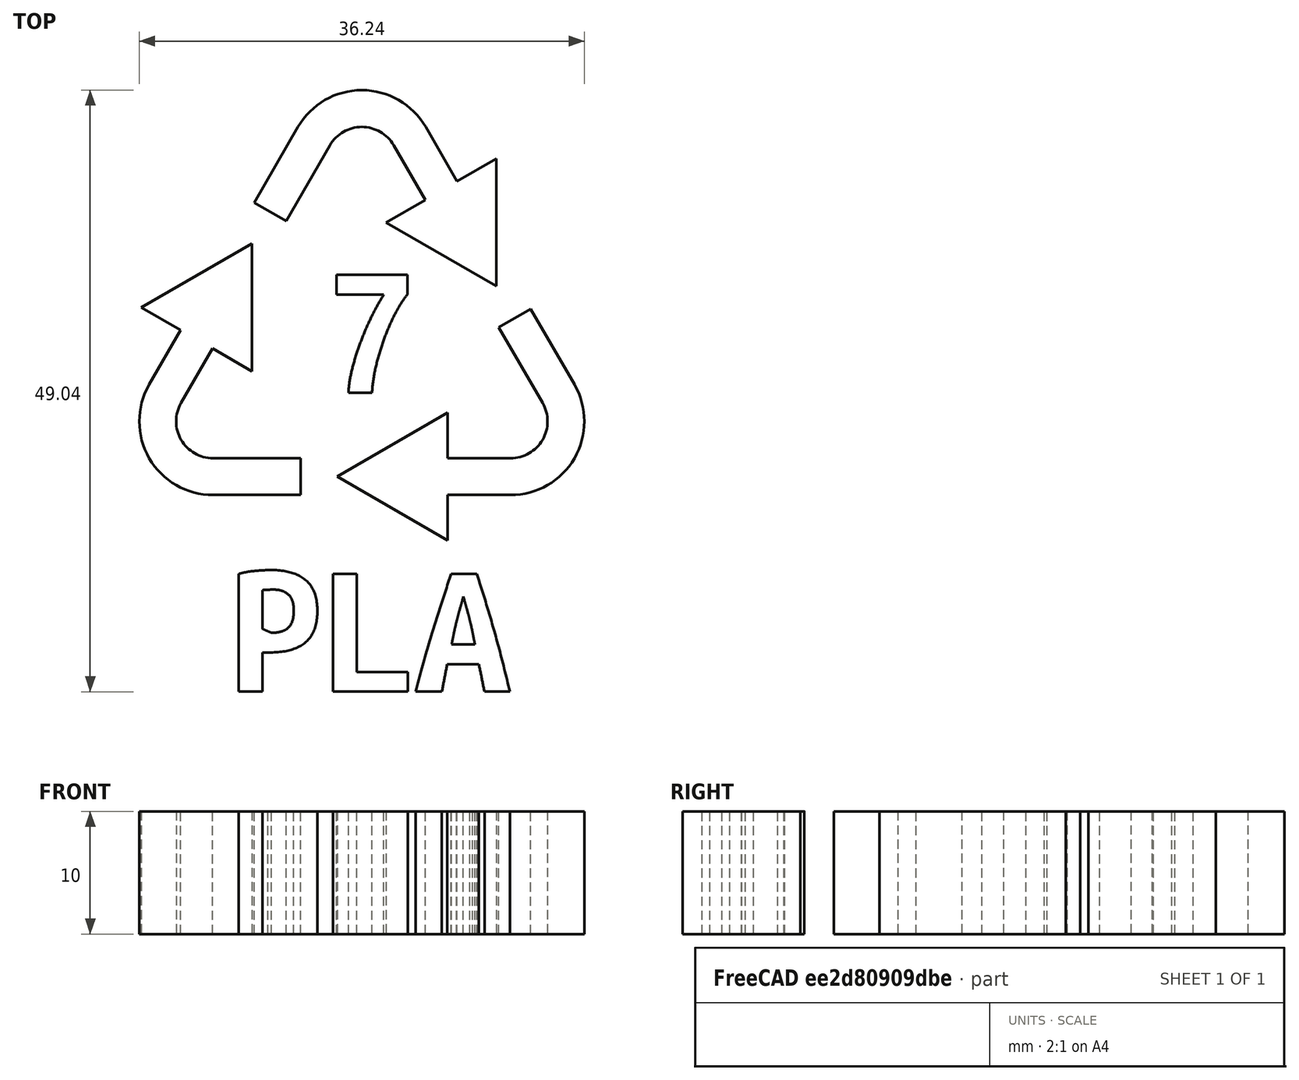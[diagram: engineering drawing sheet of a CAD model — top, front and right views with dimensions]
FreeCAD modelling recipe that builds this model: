
FCSTD DOCUMENT  (FreeCAD 0.17R13541 (Git))
Label: PLA-recycling-symbol
License: All rights reserved
LicenseURL: http://en.wikipedia.org/wiki/All_rights_reserved
objects: Part::Extrusion×5, Part::Fillet×5, Part::Feature×4, Part::MultiFuse×4, Part::RegularPolygon×3, Part::Part2DObjectPython×2, Part::Cut×2, Part::FeaturePython×2, Part::Box×1, App::DocumentObjectGroup×1
note: 28 computed .brp shape members not serialized (recipe doc carries the construction recipe); baked Part::Feature solids carry a one-line shape summary decoded from their .brp

FEATURE [Part::Part2DObjectPython] ShapeString  # Draft 2D object (typed FeaturePython)
  FontFile = <userpath>/Desktop/rrlOwncloud/Libraries-and-settings/Fonts/ubuntu-font-family-0.80/UbuntuMono-B.ttf
  Placement = pos=(-45.93,-118.03,0) rot=(0.707107,-0.707107,0;3.14159rad)
  Size = 10
  String = PLA
  Tracking = 0
FEATURE [Part::Extrusion] Extrude  label="PLA-1"
  Base = -> ShapeString
  Dir = (0,0,-1)
  DirMode = 2
  FaceMakerClass = Part::FaceMakerBullseye
  LengthFwd = 10
  LengthRev = 0
  Placement = pos=(-142,-85,0) rot=(-0.707107,0.707107,0;3.14159rad)
  Solid = false
  Symmetric = false
FEATURE [Part::Part2DObjectPython] ShapeString001  # Draft 2D object (typed FeaturePython)
  FontFile = <userpath>/Desktop/rrlOwncloud/Libraries-and-settings/Fonts/ubuntu-font-family-0.80/UbuntuMono-B.ttf
  Placement = pos=(87.32,101.38,0) rot=(0.707107,-0.707107,0;3.14159rad)
  Size = 10
  String = 7
  Tracking = 0
FEATURE [Part::Extrusion] Extrude001  label="7-1"
  Base = -> ShapeString001
  Dir = (0,0,-1)
  DirMode = 2
  FaceMakerClass = Part::FaceMakerBullseye
  LengthFwd = 10
  LengthRev = 0
  Placement = pos=(95,78,0) rot=(-0.707107,0.707107,0;3.14159rad)
  Solid = false
  Symmetric = false
FEATURE [Part::RegularPolygon] RegularPolygon  label="Regular polygon"
  AttacherType = Attacher::AttachEngine3D
  Circumradius = 20
  Placement = pos=(0,0,0) rot=(0,0,1;1.5708rad)
  Polygon = 3
FEATURE [Part::RegularPolygon] RegularPolygon001  label="Regular polygon001"
  AttacherType = Attacher::AttachEngine3D
  Circumradius = 26
  Placement = pos=(0,0,0) rot=(0,0,1;1.5708rad)
  Polygon = 3
FEATURE [Part::Extrusion] Extrude002
  Base = -> RegularPolygon001
  Dir = (0,0,1)
  DirMode = 2
  FaceMakerClass = Part::FaceMakerBullseye
  LengthFwd = 10
  LengthRev = 0
  Solid = true
  Symmetric = false
FEATURE [Part::Extrusion] Extrude003
  Base = -> RegularPolygon
  Dir = (0,0,1)
  DirMode = 2
  FaceMakerClass = Part::FaceMakerBullseye
  LengthFwd = 12
  LengthRev = 0
  Placement = pos=(0,0,-1) rot=(0,0,1;0rad)
  Solid = true
  Symmetric = false
FEATURE [Part::Cut] Cut
  Base = -> Extrude002
  Tool = -> Extrude003
FEATURE [Part::Fillet] Fillet
  Base = -> Cut
  Edges = 1 edges r=3: [Edge18]
FEATURE [Part::Fillet] Fillet001
  Base = -> Fillet
  Edges = 1 edges r=6: [Edge16]
FEATURE [Part::Fillet] Fillet002
  Base = -> Fillet001
  Edges = 1 edges r=3: [Edge18]
FEATURE [Part::Fillet] Fillet003
  Base = -> Fillet002
  Edges = 1 edges r=3: [Edge17]
FEATURE [Part::Fillet] Fillet004  label="triangle-ring"
  Base = -> Fillet003
  Edges = 2 edges r=6: [Edge24,Edge28]
FEATURE [Part::RegularPolygon] RegularPolygon002  label="Regular polygon002"
  AttacherType = Attacher::AttachEngine3D
  Circumradius = 6
  Polygon = 3
FEATURE [Part::Extrusion] Extrude004  label="arrow"
  Base = -> RegularPolygon002
  Dir = (0,0,1)
  DirMode = 2
  FaceMakerClass = Part::FaceMakerBullseye
  LengthFwd = 10
  LengthRev = 0
  Placement = pos=(-4,-11.5,0) rot=(0,0,1;0rad)
  Solid = true
  Symmetric = false
FEATURE [Part::Feature] Extrude004001
  Placement = pos=(11.9593,2.2859,0) rot=(0,0,1;2.0944rad)
  shape: bbox 9 x 10.39 x 10 mm, 5 faces (baked)
FEATURE [Part::Feature] Extrude004002
  Placement = pos=(-7.95929,9.2141,0) rot=(0,0,1;4.18879rad)
  shape: bbox 9 x 10.39 x 10 mm, 5 faces (baked)
FEATURE [Part::Box] Box001  label="Cube001"
  AttacherType = Attacher::AttachEngine3D
  Height = 16
  Length = 10
  Placement = pos=(-5,-17,-4) rot=(0,0,1;0rad)
  Width = 10
FEATURE [Part::Feature] Box001001
  Placement = pos=(17.2224,4.16987,-4) rot=(0,0,1;2.0944rad)
  shape: bbox 13.66 x 13.66 x 16 mm, 6 faces (baked)
FEATURE [Part::Feature] Box001002
  Placement = pos=(-12.2224,12.8301,-4) rot=(0,0,1;4.18879rad)
  shape: bbox 13.66 x 13.66 x 16 mm, 6 faces (baked)
FEATURE [Part::MultiFuse] Fusion  label="gaps"
  Shapes = -> [Box001,Box001001,Box001002]
FEATURE [Part::Cut] Cut001
  Base = -> Fillet004
  Tool = -> Fusion
FEATURE [Part::MultiFuse] Fusion001  label="arrows"
  Shapes = -> [Extrude004,Extrude004002,Extrude004001]
FEATURE [Part::MultiFuse] Fusion002  label="recycle"
  Placement = pos=(0,0,10) rot=(0,1,0;3.14159rad)
  Shapes = -> [Cut001,Fusion001]
FEATURE [Part::FeaturePython] Clone  label="7"  # Draft clone (typed FeaturePython)
  AttacherType = Attacher::AttachEngine3D
  Fuse = false
  Objects = -> [Extrude001]
  Placement = pos=(48,39,0) rot=(-0.707107,0.707107,0;3.14159rad)
  Scale = (0.5,0.5,1)
FEATURE [Part::FeaturePython] Clone001  label="PLA"  # Draft clone (typed FeaturePython)
  AttacherType = Attacher::AttachEngine3D
  Fuse = false
  Objects = -> [Extrude]
  Placement = pos=(-70,-52,0) rot=(-0.707107,0.707107,0;3.14159rad)
  Scale = (0.5,0.5,1)
FEATURE [App::DocumentObjectGroup] Group  label="Construction"
  Group = -> [Extrude,Extrude001]
FEATURE [Part::MultiFuse] Fusion003  label="PLA-recycling-symbol"
  Shapes = -> [Fusion002,Clone001,Clone]
